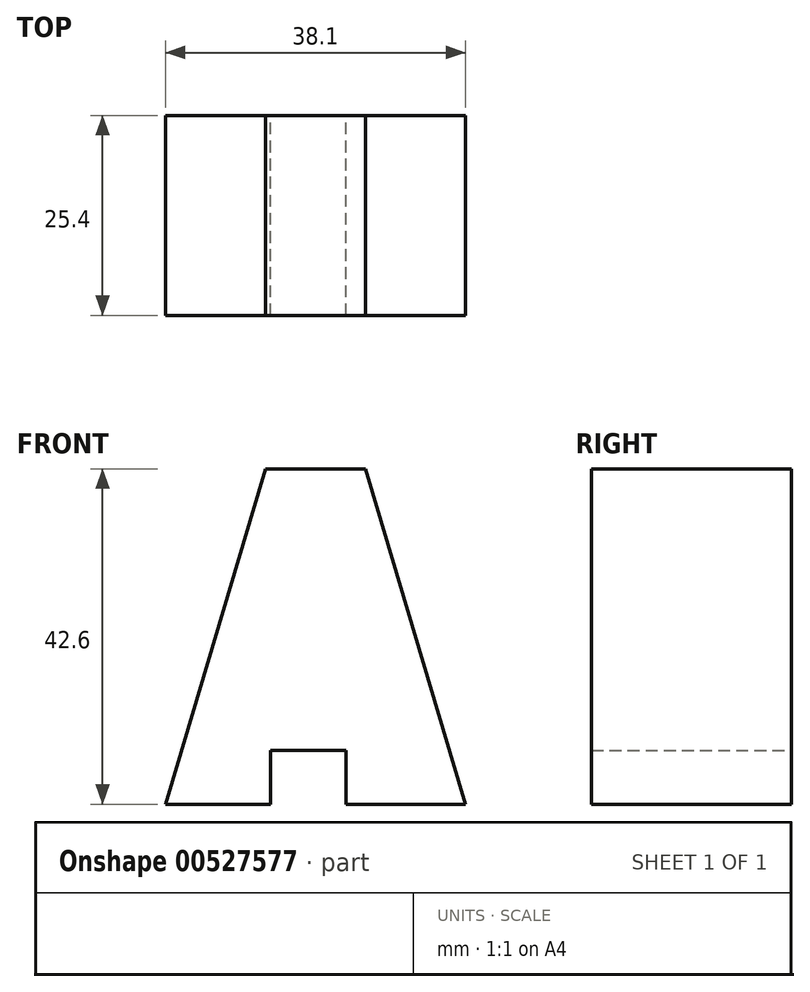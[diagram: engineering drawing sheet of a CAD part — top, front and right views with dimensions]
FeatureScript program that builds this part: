
annotation { "Feature Type Name" : "Feature", "Feature Type Description" : "" }
export const myFeature = defineFeature(function(context is Context, id is Id, definition is map)
    precondition{}
    {
        {
            var Q0;
            Q0=qCreatedBy(makeId("Front.planeOp"),FACE);
            var sketch = newSketch(context, id + "F0", { "sketchPlane" : qUnion([Q0])});
            skLineSegment(sketch, "E0", {"start": v(27.63, 0) * mm, "end": v(40.33, 42.6) * mm});
            skLineSegment(sketch, "E1", {"start": v(53.03, 42.6) * mm, "end": v(40.33, 42.6) * mm});
            skLineSegment(sketch, "E2", {"start": v(53.03, 42.6) * mm, "end": v(65.73, 0) * mm});
            skLineSegment(sketch, "E3", {"start": v(27.63, 0) * mm, "end": v(65.73, 0) * mm});
            skLineSegment(sketch, "E4", {"start": v(40.94, 0) * mm, "end": v(40.94, 6.82) * mm});
            skLineSegment(sketch, "E5", {"start": v(40.94, 6.82) * mm, "end": v(50.55, 6.82) * mm});
            skLineSegment(sketch, "E6", {"start": v(50.55, 0) * mm, "end": v(50.55, 6.82) * mm});
            skSolve(sketch);
        }
        {
            var Q0;
            {var subQ1=sQuery(id+"F0.wireOp",EDGE,"E0");Q0=makeQuery(id+"F0.imprint","IMPRINT",FACE,{"disambiguationData":[TD([[makeQuery(id+"F0.imprint","IMPRINT",EDGE,{"derivedFrom":subQ1}),-1.0]])]});}
            extrude(context, id + "F1", {"entities" : qUnion([Q0]), "depth" : 25.4 * mm, "offsetDistance" : 25.4 * mm});
        }
    });
